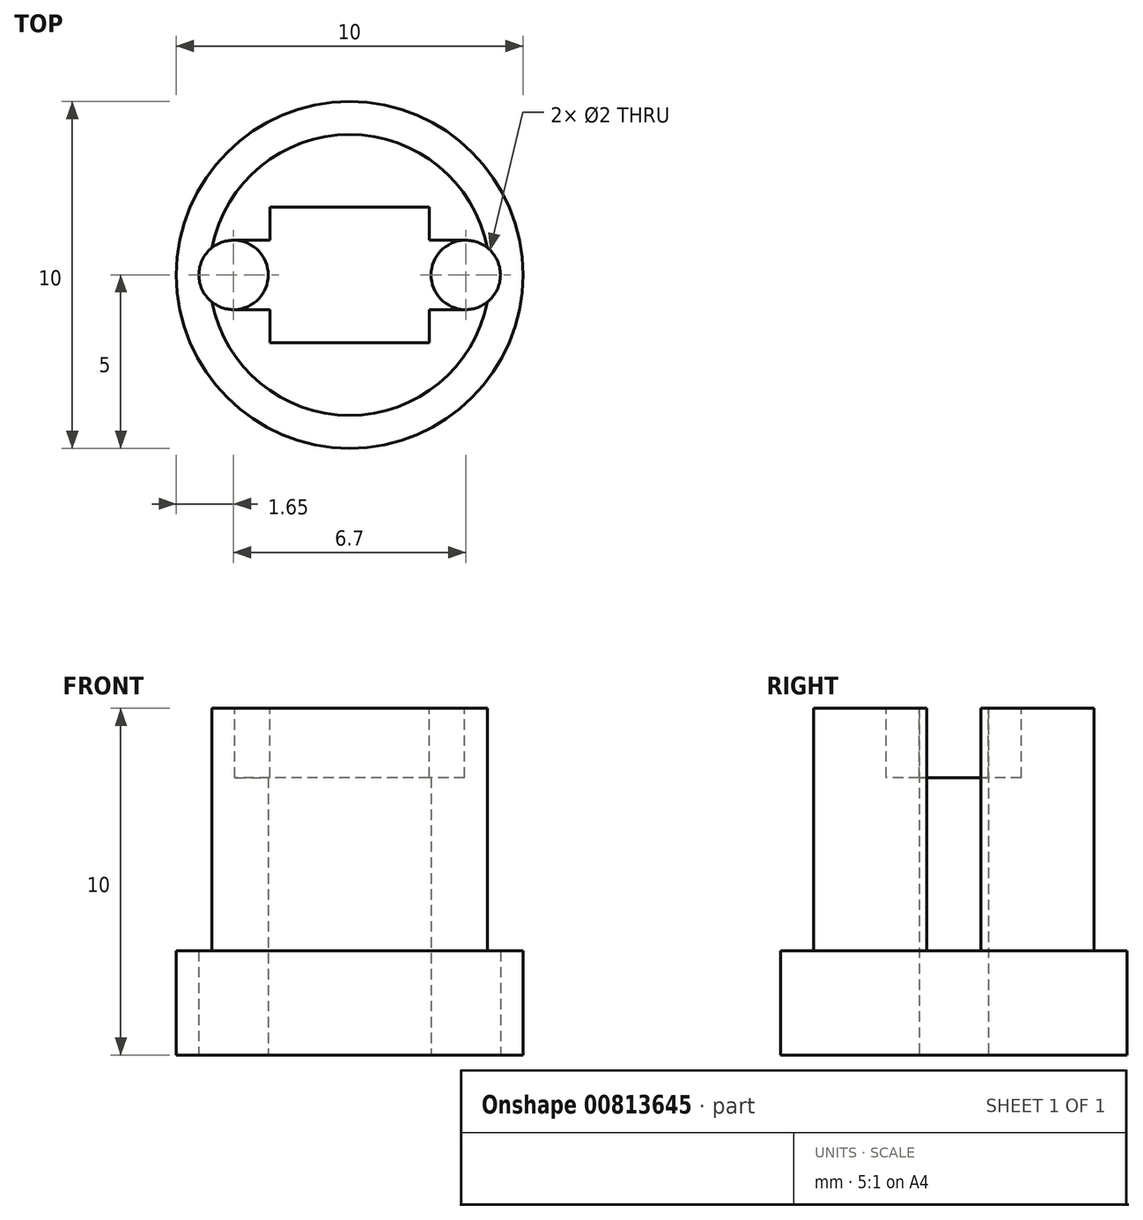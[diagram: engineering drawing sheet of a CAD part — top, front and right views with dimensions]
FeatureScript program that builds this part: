
annotation { "Feature Type Name" : "Feature", "Feature Type Description" : "" }
export const myFeature = defineFeature(function(context is Context, id is Id, definition is map)
    precondition{}
    {
        {
            var Q0;
            Q0=qCreatedBy(makeId("Top.planeOp"),FACE);
            var sketch = newSketch(context, id + "F0", { "sketchPlane" : qUnion([Q0])});
            skCircle(sketch, "E0", {"center": v(0, 0) * mm, "radius": 5 * mm});
            skSolve(sketch);
        }
        {
            var Q0;
            Q0=makeQuery(id+"F0.imprint","IMPRINT",FACE,{"disambiguationData":[TD([[makeQuery(id+"F0.imprint","IMPRINT",EDGE,{"derivedFrom":sQuery(id+"F0.wireOp",EDGE,"E0")}),1.0]])]});
            extrude(context, id + "F1", {"entities" : qUnion([Q0]), "depth" : 3 * mm, "offsetDistance" : 25 * mm});
        }
        {
            var Q0;
            Q0=qCreatedBy(makeId("Top.planeOp"),FACE);
            var sketch = newSketch(context, id + "F2", { "sketchPlane" : qUnion([Q0])});
            skCircle(sketch, "E1", {"center": v(0, 0) * mm, "radius": 4.05 * mm});
            skCircle(sketch, "E2", {"center": v(-3.35, 0) * mm, "radius": 1 * mm});
            skCircle(sketch, "E3.MirrorC", {"center": v(3.35, 0) * mm, "radius": 1 * mm});
            skSolve(sketch);
        }
        {
            var Q0;
            {var subQ0=sQuery(id+"F2.wireOp",EDGE,"E2");var subQ1=sQuery(id+"F2.wireOp",EDGE,"E1");var subQ2=makeQuery(id+"F2.imprint","INTERSECT",VERTEX,{"disambiguationData":[OD(0.0)],"derivedFrom":[subQ1,subQ0]});Q0=makeQuery(id+"F2.imprint","IMPRINT",FACE,{"disambiguationData":[TD([[makeQuery(id+"F2.imprint","IMPRINT",EDGE,{"disambiguationData":[TD([[subQ2,1.0]])],"derivedFrom":subQ1}),1.0]])]});}
            extrude(context, id + "F3", {"entities" : qUnion([Q0]), "operationType" : NewBodyOperationType.ADD, "depth" : 10 * mm, "offsetDistance" : 25 * mm});
        }
        {
            var Q0;
            Q0=makeQuery(id+"F3.opExtrude","CAP_FACE",FACE,{"disambiguationData":[OSD([sQuery(id+"F2.wireOp",EDGE,"E1"),sQuery(id+"F2.wireOp",EDGE,"E2"),sQuery(id+"F2.wireOp",EDGE,"E3.MirrorC")])],"isStart":false});
            var sketch = newSketch(context, id + "F4", { "sketchPlane" : qUnion([Q0])});
            skLineSegment(sketch, "E4.bottom", {"start": v(2.3, 1.95) * mm, "end": v(-2.3, 1.95) * mm});
            skLineSegment(sketch, "E4.top", {"start": v(2.3, -1.95) * mm, "end": v(-2.3, -1.95) * mm});
            skLineSegment(sketch, "E4.left", {"start": v(2.3, 1.95) * mm, "end": v(2.3, -1.95) * mm});
            skLineSegment(sketch, "E4.right", {"start": v(-2.3, 1.95) * mm, "end": v(-2.3, -1.95) * mm});
            skPoint(sketch, "E4.middle", {"position": v(0, 0) * mm});
            skLineSegment(sketch, "E5.bottom", {"start": v(3.39, 1) * mm, "end": v(-3.39, 1) * mm});
            skLineSegment(sketch, "E5.top", {"start": v(3.39, -1) * mm, "end": v(-3.39, -1) * mm});
            skLineSegment(sketch, "E5.left", {"start": v(3.39, 1) * mm, "end": v(3.39, -1) * mm});
            skLineSegment(sketch, "E5.right", {"start": v(-3.39, 1) * mm, "end": v(-3.39, -1) * mm});
            skSolve(sketch);
        }
        {
            var Q0;
            {var subQ0=sQuery(id+"F4.wireOp",EDGE,"E4.bottom");Q0=makeQuery(id+"F4.imprint","IMPRINT",FACE,{"disambiguationData":[TD([[makeQuery(id+"F4.imprint","IMPRINT",EDGE,{"derivedFrom":subQ0}),1.0]])]});}
            var Q1;
            {var subQ0=sQuery(id+"F4.wireOp",EDGE,"E4.top");Q1=makeQuery(id+"F4.imprint","IMPRINT",FACE,{"disambiguationData":[TD([[makeQuery(id+"F4.imprint","IMPRINT",EDGE,{"derivedFrom":subQ0}),-1.0]])]});}
            var Q2;
            {var subQ0=sQuery(id+"F4.wireOp",EDGE,"E5.bottom");var subQ1=sQuery(id+"F4.wireOp",EDGE,"E4.left");var subQ2=makeQuery(id+"F4.imprint","INTERSECT",VERTEX,{"derivedFrom":[subQ1,subQ0]});Q2=makeQuery(id+"F4.imprint","IMPRINT",FACE,{"disambiguationData":[TD([[makeQuery(id+"F4.imprint","IMPRINT",EDGE,{"disambiguationData":[TD([[subQ2,-1.0]])],"derivedFrom":subQ1}),1.0]])]});}
            var Q3;
            {var subQ0=sQuery(id+"F4.wireOp",EDGE,"E5.bottom");var subQ1=sQuery(id+"F4.wireOp",EDGE,"E4.right");var subQ2=makeQuery(id+"F4.imprint","INTERSECT",VERTEX,{"derivedFrom":[subQ1,subQ0]});Q3=makeQuery(id+"F4.imprint","IMPRINT",FACE,{"disambiguationData":[TD([[makeQuery(id+"F4.imprint","IMPRINT",EDGE,{"disambiguationData":[TD([[subQ2,-1.0]])],"derivedFrom":subQ1}),-1.0]])]});}
            var Q4;
            {var subQ0=sQuery(id+"F4.wireOp",EDGE,"E5.bottom");var subQ1=sQuery(id+"F4.wireOp",EDGE,"E4.left");var subQ2=makeQuery(id+"F4.imprint","INTERSECT",VERTEX,{"derivedFrom":[subQ1,subQ0]});Q4=makeQuery(id+"F4.imprint","IMPRINT",FACE,{"disambiguationData":[TD([[makeQuery(id+"F4.imprint","IMPRINT",EDGE,{"disambiguationData":[TD([[subQ2,-1.0]])],"derivedFrom":subQ1}),-1.0]])]});}
            extrude(context, id + "F5", {"entities" : qUnion([Q0, Q1, Q2, Q3, Q4]), "operationType" : NewBodyOperationType.REMOVE, "oppositeDirection" : true, "depth" : 2 * mm, "offsetDistance" : 25 * mm});
        }
        {
            var Q0;
            {var subQ0=sQuery(id+"F2.wireOp",EDGE,"E3.MirrorC");var subQ1=sQuery(id+"F2.wireOp",EDGE,"E1");var subQ2=makeQuery(id+"F2.imprint","INTERSECT",VERTEX,{"disambiguationData":[OD(0.0)],"derivedFrom":[subQ1,subQ0]});Q0=makeQuery(id+"F2.imprint","IMPRINT",FACE,{"disambiguationData":[TD([[makeQuery(id+"F2.imprint","IMPRINT",EDGE,{"disambiguationData":[TD([[subQ2,1.0]])],"derivedFrom":subQ1}),1.0]])]});}
            var Q1;
            {var subQ0=sQuery(id+"F2.wireOp",EDGE,"E2");var subQ1=sQuery(id+"F2.wireOp",EDGE,"E1");var subQ2=makeQuery(id+"F2.imprint","INTERSECT",VERTEX,{"disambiguationData":[OD(0.0)],"derivedFrom":[subQ1,subQ0]});Q1=makeQuery(id+"F2.imprint","IMPRINT",FACE,{"disambiguationData":[TD([[makeQuery(id+"F2.imprint","IMPRINT",EDGE,{"disambiguationData":[TD([[subQ2,-1.0]])],"derivedFrom":subQ1}),1.0]])]});}
            var Q2;
            {var subQ0=sQuery(id+"F2.wireOp",EDGE,"E2");var subQ1=sQuery(id+"F2.wireOp",EDGE,"E1");var subQ2=makeQuery(id+"F2.imprint","INTERSECT",VERTEX,{"disambiguationData":[OD(0.0)],"derivedFrom":[subQ1,subQ0]});Q2=makeQuery(id+"F2.imprint","IMPRINT",FACE,{"disambiguationData":[TD([[makeQuery(id+"F2.imprint","IMPRINT",EDGE,{"disambiguationData":[TD([[subQ2,-1.0]])],"derivedFrom":subQ1}),-1.0]])]});}
            var Q3;
            {var subQ0=sQuery(id+"F2.wireOp",EDGE,"E3.MirrorC");var subQ1=sQuery(id+"F2.wireOp",EDGE,"E1");var subQ2=makeQuery(id+"F2.imprint","INTERSECT",VERTEX,{"disambiguationData":[OD(0.0)],"derivedFrom":[subQ1,subQ0]});Q3=makeQuery(id+"F2.imprint","IMPRINT",FACE,{"disambiguationData":[TD([[makeQuery(id+"F2.imprint","IMPRINT",EDGE,{"disambiguationData":[TD([[subQ2,1.0]])],"derivedFrom":subQ1}),-1.0]])]});}
            extrude(context, id + "F6", {"entities" : qUnion([Q0, Q1, Q2, Q3]), "operationType" : NewBodyOperationType.REMOVE, "depth" : 3 * mm, "offsetDistance" : 25 * mm});
        }
    });
